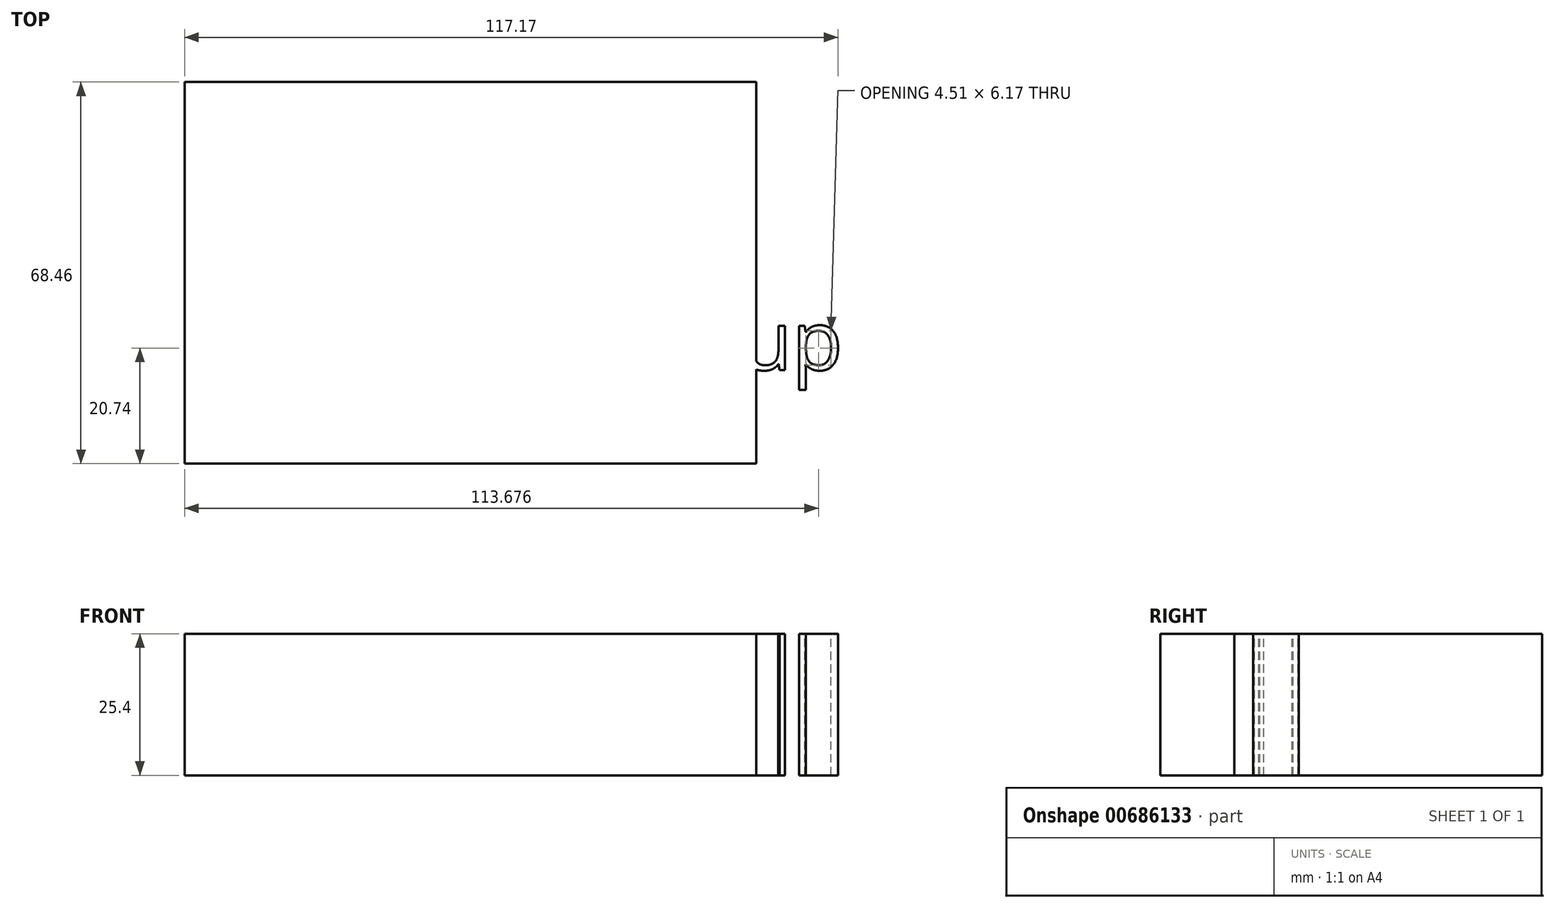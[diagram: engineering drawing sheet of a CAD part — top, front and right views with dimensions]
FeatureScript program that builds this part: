
annotation { "Feature Type Name" : "Feature", "Feature Type Description" : "" }
export const myFeature = defineFeature(function(context is Context, id is Id, definition is map)
    precondition{}
    {
        {
            var Q0;
            Q0=qCreatedBy(makeId("Top.planeOp"),FACE);
            var sketch = newSketch(context, id + "F0", { "sketchPlane" : qUnion([Q0])});
            skLineSegment(sketch, "E0.bottom", {"start": v(-54.56, 51.66) * mm, "end": v(47.92, 51.66) * mm});
            skLineSegment(sketch, "E0.top", {"start": v(-54.56, -16.8) * mm, "end": v(47.92, -16.8) * mm});
            skLineSegment(sketch, "E0.left", {"start": v(-54.56, 51.66) * mm, "end": v(-54.56, -16.8) * mm});
            skLineSegment(sketch, "E0.right", {"start": v(47.92, 51.66) * mm, "end": v(47.92, -16.8) * mm});
            skSolve(sketch);
        }
        {
            var Q0;
            Q0 = qSketchRegion(id + "F0", true);
            extrude(context, id + "F1", {"entities" : qUnion([Q0]), "depth" : 25.4 * mm, "offsetDistance" : 25.4 * mm});
        }
        {
            var Q0;
            Q0=makeQuery(id+"F1.opExtrude","CAP_FACE",FACE,{"disambiguationData":[OSD([sQuery(id+"F0.wireOp",EDGE,"E0.bottom"),sQuery(id+"F0.wireOp",EDGE,"E0.top"),sQuery(id+"F0.wireOp",EDGE,"E0.left"),sQuery(id+"F0.wireOp",EDGE,"E0.right")])],"isStart":false});
            var sketch = newSketch(context, id + "F2", { "sketchPlane" : qUnion([Q0])});
            skText(sketch, "E1", { "text": "yo what up", "fontName": "OpenSans-Regular.ttf"});
            const initialGuessF2  = {"E1": [-0.0126, 0, 1, 0, 0.01062]};
            skSetInitialGuess(sketch, initialGuessF2);
            skSolve(sketch);
        }
        {
            var Q0;
            Q0 = qSketchRegion(id + "F2", true);
            extrude(context, id + "F3", {"entities" : qUnion([Q0]), "operationType" : NewBodyOperationType.ADD, "oppositeDirection" : true, "depth" : 25.4 * mm, "offsetDistance" : 25.4 * mm});
        }
    });
